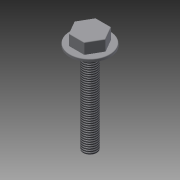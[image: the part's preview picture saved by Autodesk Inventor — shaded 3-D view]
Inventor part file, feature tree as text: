
AUTODESK INVENTOR PART (.ipt)
format: ipt  version: 2015 (Build 190159000, 159)  size: 126,976 bytes
history: native  units: mm
features: extrude x3, sketch x3, fillet x1, thread x1, chamfer x1
ambient origin geometry x8: Origin, YZ Plane, XZ Plane, XY Plane, X Axis, Y Axis, Z Axis, Center Point
bodies: 实体1 (feature_tree)
feature tree (9):
  extrude  "拉伸1"  Depth=2.0mm TaperAngle=0.0deg
  extrude  "拉伸2"  Depth=20.0mm
  fillet  "圆角1"  Radius=8.0mm
  extrude  "拉伸3"  Depth=10.0mm
  thread  "螺纹1"  [1 undecoded]
  chamfer  "倒角1"  Distance=10.0mm
  sketch  "草图1"  dims[d0=30.0mm d1=2.0mm d2=0.0mm]
  sketch  "草图2"  dims[d3=3.02274mm d4=20.0mm d5=8.0mm d6=0.0mm]
  sketch  "草图3"  dims[d7=0.5mm d8=10.0mm d9=67.0mm d10=0.0mm d11=10.0mm d12=0.0mm d13=0.5mm d14=2.0mm d15=45.0deg]
note: 1 required parameter value undecoded (feature->parameter linkage not recoverable at this tier; creation-order binding heuristic only, values carry confidence <= 0.55)
